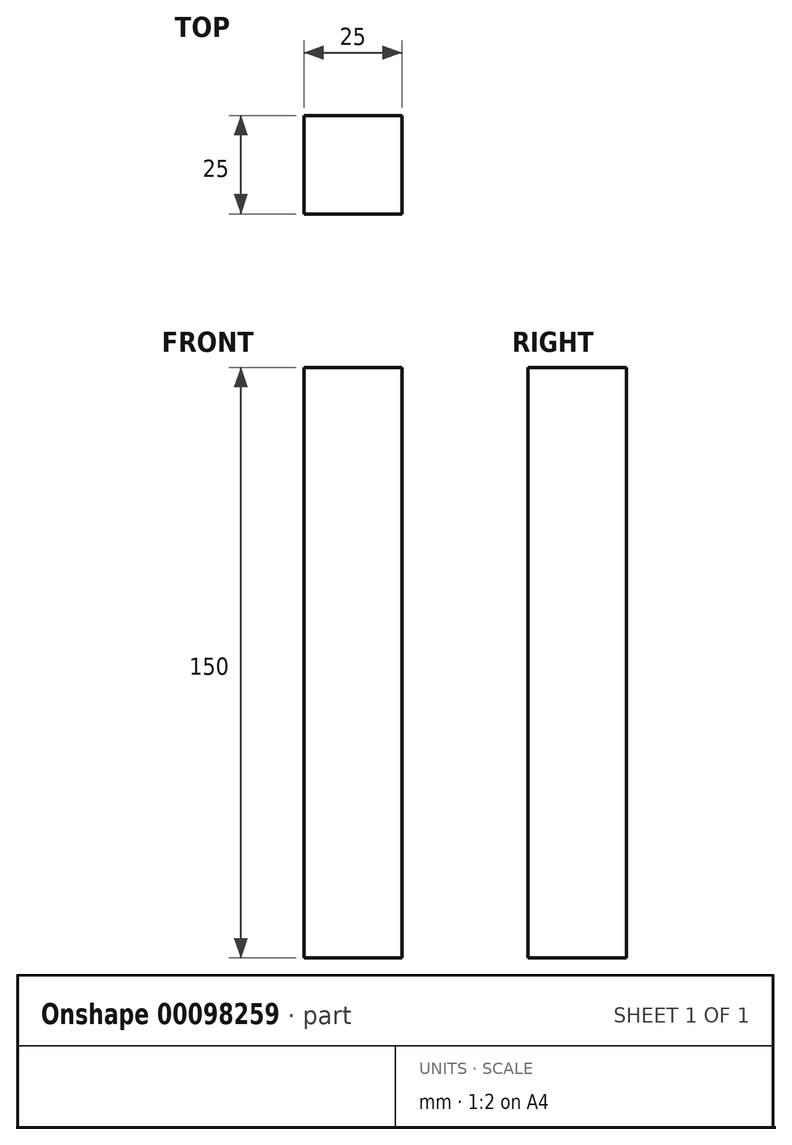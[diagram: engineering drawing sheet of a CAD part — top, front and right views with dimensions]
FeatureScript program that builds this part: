
annotation { "Feature Type Name" : "Feature", "Feature Type Description" : "" }
export const myFeature = defineFeature(function(context is Context, id is Id, definition is map)
    precondition{}
    {
        {
            var Q0;
            Q0=qCreatedBy(makeId("Top.planeOp"),FACE);
            var sketch = newSketch(context, id + "F0", { "sketchPlane" : qUnion([Q0])});
            skLineSegment(sketch, "E0.bottom", {"start": v(-11.08, 14.14) * mm, "end": v(13.92, 14.14) * mm});
            skLineSegment(sketch, "E0.top", {"start": v(-11.08, -10.86) * mm, "end": v(13.92, -10.86) * mm});
            skLineSegment(sketch, "E0.left", {"start": v(-11.08, 14.14) * mm, "end": v(-11.08, -10.86) * mm});
            skLineSegment(sketch, "E0.right", {"start": v(13.92, 14.14) * mm, "end": v(13.92, -10.86) * mm});
            skSolve(sketch);
        }
        {
            var Q0;
            Q0=makeQuery(id+"F0.imprint","IMPRINT",FACE,{"disambiguationData":[TD([[makeQuery(id+"F0.imprint","IMPRINT",EDGE,{"derivedFrom":sQuery(id+"F0.wireOp",EDGE,"E0.bottom")}),-1.0]])]});
            extrude(context, id + "F1", {"entities" : qUnion([Q0]), "depth" : 150 * mm});
        }
    });
